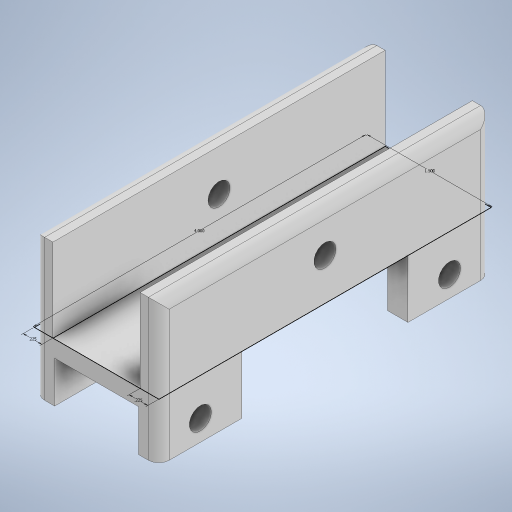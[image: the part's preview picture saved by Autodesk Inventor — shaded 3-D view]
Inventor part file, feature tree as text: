
AUTODESK INVENTOR PART (.ipt)
format: ipt  version: 2024.1 (Build 281209000, 209)  size: 297,472 bytes
history: native  units: in
note: dims shown in document units (in); Inventor stores cm internally (conversion verified against a paired STEP export)
features: extrude x4, sketch x3, hole x2, fillet x1
ambient origin geometry x8: Origin, YZ Plane, XZ Plane, XY Plane, X Axis, Y Axis, Z Axis, Center Point
bodies: Solid1 (feature_tree)
feature tree (10):
  extrude  "Extrusion1"  Depth=4.0in
  extrude  "Extrusion2"  Depth=0.225in
  hole  "Hole1"  [1 undecoded]
  extrude  "Extrusion3"  Depth=0.5in
  hole  "Hole2"  [1 undecoded]
  fillet  "Fillet1"  Radius=4.0in
  extrude  "Extrusion4"  Depth=0.245in
  sketch  "Sketch3"  dims[d0=1.5in d1=4.0in]
  sketch  "Sketch4"  dims[d2=0.225in d3=0.225in]
  sketch  "Sketch5"  dims[d4=1.0in d5=0.0in d6=0.2in d7=0.0in d8=0.5in d9=0.266in d10=0.75in d11=0.438in d12=0.25in d13=0.5635in d14=1.0in d15=0.8108in d16=0.245in d17=4.0in d18=0.245in d19=0.5in d20=0.0in d21=0.5in d22=0.25in d23=0.5in d24=0.266in d25=0.043in d26=0.438in d27=0.25in d28=0.5635in d29=1.0in d30=0.8108in d31=0.125in d32=2.0in d33=1.0in d34=0.0in]
note: 2 required parameter values undecoded (feature->parameter linkage not recoverable at this tier; creation-order binding heuristic only, values carry confidence <= 0.55)
